# Revit family: PRD_AR_ShwrCrtnRls_MEDCARECurtainRod_MEDC0014_MEDC0015
name_source: partatom
category: Specialty Equipment
units: mm (PartAtom-declared; Revit-internal decimal feet)

## family parameters
Cut with Voids When Loaded = No
Enable Cutting in Views = No
Host = Face
Maintain Annotation Orientation = No
OmniClass Number = 23.40.20.21.44
OmniClass Title = Shower Rods, Curtains
Part Type = Normal
Room Calculation Point = No
Round Connector Dimension = Use Diameter
Shared = No

## types (2) — shared parameters
AssetType = Fixed
Back = no
BodyMaterial = PRD_AR_StainlessSteel_SatinFinished_BasaltGrey
Category = Pr_40_30_20_77, Shower curtain rails
Color = basalt grey
Default Elevation = 1200 mm
Description = MEDCARE curtain rod, for wall and ceiling mounting, stainless steel, basalt grey coated surface, 27 mm pipe diameter, 1.5 mm material thickness, consisting of two horizontal rods joined at a right angle and one ceiling mounting. Curtain rod and ceiling mounting can be shortened on site if necessary, stainless steel mounting cylinder, satin finish surface, curtain rings included, white colour, including mounting material.
Diameter = 27 mm  [stored 0.0885827 ft]
Export Type to IFC As = IfcRailingType
Finish = satin finished
IfcExportAs = IfcRailingType
IfcExportType = USERDEFINED
IsExternal = FALSE
Manufacturer = KWC Group Management AG
ManufacturerName = KWC Group Management AG
ManufacturerURL = www.kwc-professional.com
Material = stainless steel
MaterialCode = 1.4301 Chrome Nickel steel V2A
NBSDescription = Shower curtain rails
NBSReference = 45-35-70/334
NominalHeight = 600 mm
OverallHeight = 680 mm
ProductInformation = http://pim.kwc.com
Status = New
SurfaceFinish = satin finished
Type IFC Predefined Type = USERDEFINED
TypeOfFixing = screw
TypeOfMounting = wall and ceiling mounting
URL = www.kwc-professional.com
Uniclass2015Code = Pr_40_30_20_77
Uniclass2015Title = Shower curtain rails
Uniclass2015Version = Products v1.36
Version = 1
zero-valued in all types: Height

## per-type parameters (varying)
| type | BIMObjectName | Features | ModelNumber | Name | NominalDepth | NominalWidth | OverallDepth | OverallWidth | Size | Width |
| MEDC0014 | PRD_AR_ShowerCurtainRails_MEDCARECurtainRod_MEDC0014 | Version for shower tray 800 x 800 mm. | 3600003784 | MEDCARE Curtain rod MEDC0014 | 800 mm  [stored 2.62467 ft] | 800 mm  [stored 2.62467 ft] | 832 mm | 832 mm | 800 x 600 x 800 mm (W x H x D) | 800 mm  [stored 2.62467 ft] |
| MEDC0015 | PRD_AR_ShowerCurtainRails_MEDCARECurtainRod_MEDC0015 | Version for shower tray 1500 x 1500 mm. | 3600003785 | MEDCARE Curtain rod MEDC0015 | 1500 mm  [stored 4.92126 ft] | 1500 mm  [stored 4.92126 ft] | 1532 mm | 1532 mm | 1500 x 600 x 1500 mm (W x H x D) | 1500 mm  [stored 4.92126 ft] |

note: column(s) folded — value = type name in every type: Model, ModelReference

note: [stored X ft] marks values corroborated as IEEE doubles in the binary element streams (Revit-internal decimal feet)

## geometry (parser evidence)
native form markers: Sweep x7
no freeform markers — native parametric forms only
